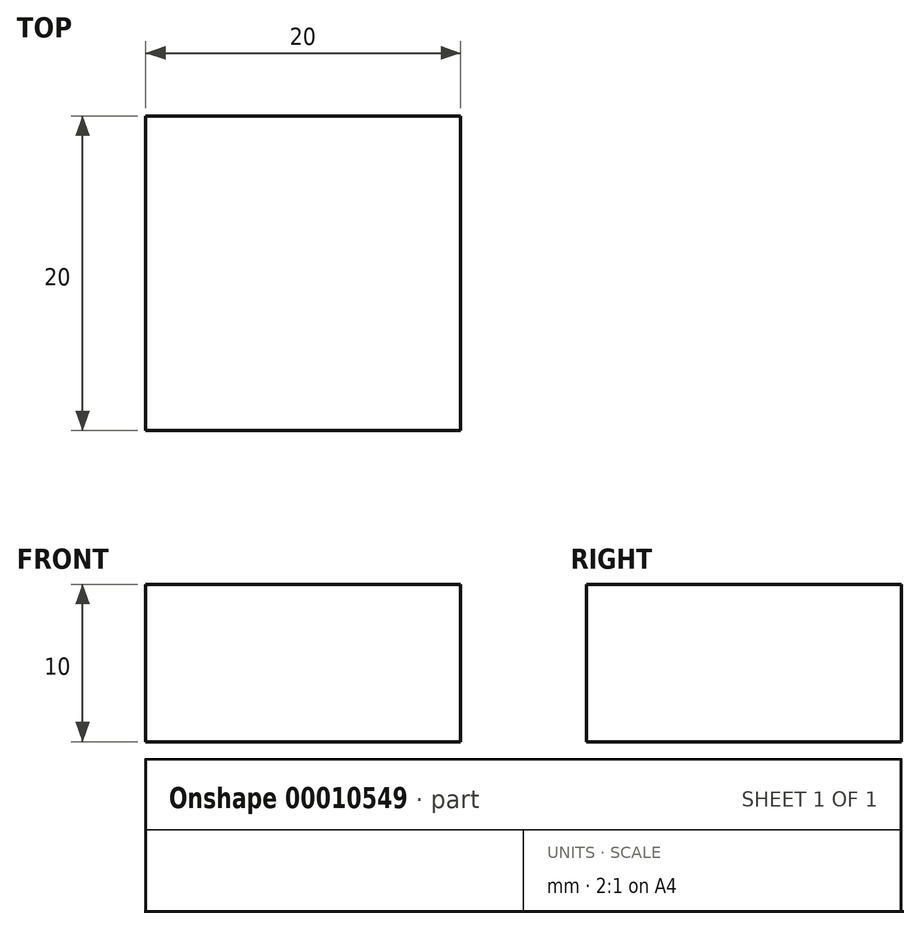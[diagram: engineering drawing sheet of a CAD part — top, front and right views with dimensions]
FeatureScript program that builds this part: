
annotation { "Feature Type Name" : "Feature", "Feature Type Description" : "" }
export const myFeature = defineFeature(function(context is Context, id is Id, definition is map)
    precondition{}
    {
        {
            var Q0;
            Q0=qCreatedBy(makeId("Top.planeOp"),FACE);
            var sketch = newSketch(context, id + "F0", { "sketchPlane" : qUnion([Q0])});
            skLineSegment(sketch, "E0.bottom", {"start": v(-9.82, 11.16) * mm, "end": v(10.18, 11.16) * mm});
            skLineSegment(sketch, "E0.top", {"start": v(-9.82, -8.84) * mm, "end": v(10.18, -8.84) * mm});
            skLineSegment(sketch, "E0.left", {"start": v(-9.82, 11.16) * mm, "end": v(-9.82, -8.84) * mm});
            skLineSegment(sketch, "E0.right", {"start": v(10.18, 11.16) * mm, "end": v(10.18, -8.84) * mm});
            skSolve(sketch);
        }
        {
            var Q0;
            Q0=makeQuery(id+"F0.imprint","IMPRINT",FACE,{"disambiguationData":[TD([[makeQuery(id+"F0.imprint","IMPRINT",EDGE,{"derivedFrom":sQuery(id+"F0.wireOp",EDGE,"E0.bottom")}),-1.0]])]});
            extrude(context, id + "F1", {"entities" : qUnion([Q0]), "depth" : 10 * mm});
        }
    });
